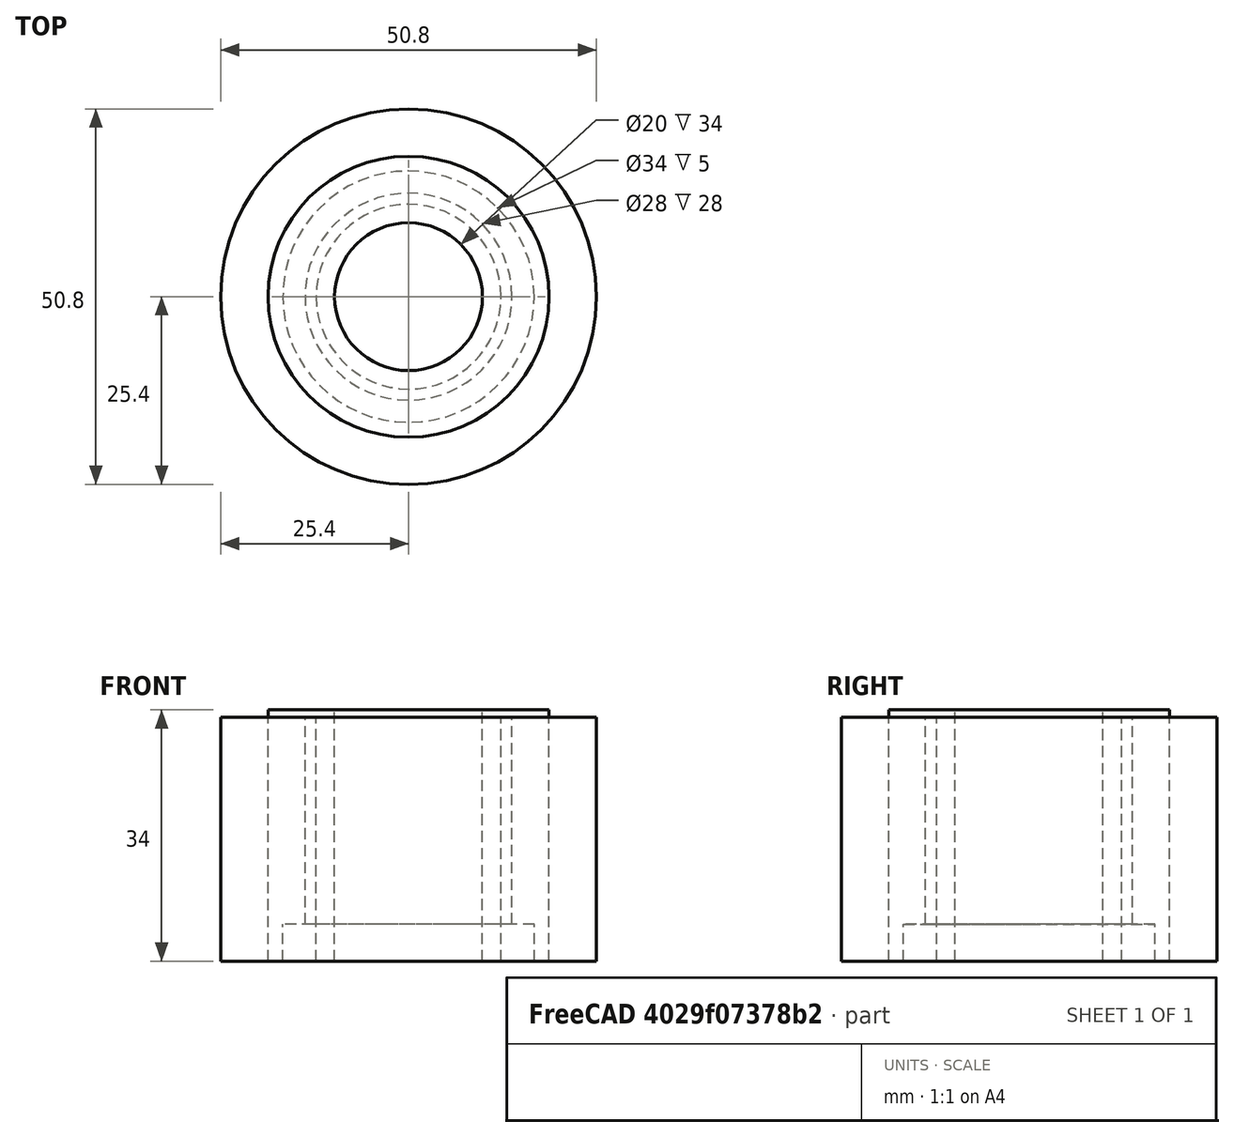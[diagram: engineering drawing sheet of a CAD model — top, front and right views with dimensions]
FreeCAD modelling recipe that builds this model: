
FCSTD DOCUMENT  (FreeCAD 0.17R13509 (Git))
Label: FTInsulator1_larger
License: All rights reserved
LicenseURL: http://en.wikipedia.org/wiki/All_rights_reserved
objects: Part::Cylinder×7, Path::FeaturePython×5, Part::Cut×3, Part::MultiFuse×2, Part::FeaturePython×2, Part::Box×1, App::FeaturePython×1, Path::FeatureCompoundPython×1
note: 18 computed .brp shape members not serialized (recipe doc carries the construction recipe); baked Part::Feature solids carry a one-line shape summary decoded from their .brp

FEATURE [Part::Cylinder] Cylinder084  label="Feedthrough005"
  Angle = 360
  AttacherType = Attacher::AttachEngine3D
  Height = 5
  Placement = pos=(73.66,148,-10) rot=(0,0,1;0rad)
  Radius = 17
  expr: Radius = 17
  expr: Placement.Base.x = 210.81999999999999 / 2 - 31.75
FEATURE [Part::Cylinder] Cylinder088  label="Feedthrough008"
  Angle = 360
  AttacherType = Attacher::AttachEngine3D
  Height = 33
  Placement = pos=(73.66,148,-10) rot=(0,0,1;0rad)
  Radius = 14
  expr: Radius = 28 / 2
  expr: Placement.Base.x = 210.81999999999999 / 2 - 31.75
FEATURE [Part::Cylinder] Cylinder090  label="FTInsInnerHole"
  Angle = 360
  AttacherType = Attacher::AttachEngine3D
  Height = 33
  Placement = pos=(73.66,148,-10) rot=(0,0,1;0rad)
  Radius = 12.5
  expr: Placement.Base.x = 210.81999999999999 / 2 - 31.75
FEATURE [Part::Box] Box016  label="FTInsLug"
  AttacherType = Attacher::AttachEngine3D
  Height = 1
  Length = 1
  Placement = pos=(63,136,-8) rot=(0,0,1;0rad)
  Width = 1
FEATURE [Part::Cylinder] Cylinder093  label="FTInsMount1"
  Angle = 360
  AttacherType = Attacher::AttachEngine3D
  Height = 14
  Placement = pos=(53.66,148,-15) rot=(0,0,1;0rad)
  Radius = 1.5
  expr: Placement.Base.x = 73.659999999999997 - 20
FEATURE [Part::Cylinder] Cylinder094  label="FTInsMount2"
  Angle = 360
  AttacherType = Attacher::AttachEngine3D
  Height = 14
  Placement = pos=(93.66,148,-14) rot=(0,0,1;0rad)
  Radius = 1.5
  expr: Placement.Base.x = 73.659999999999997 + 20
FEATURE [Part::MultiFuse] Fusion038
  Shapes = -> [Cylinder084,Cylinder088,Box016]
FEATURE [Part::MultiFuse] Fusion039
  Shapes = -> [Cylinder094,Cylinder093,Cylinder090]
FEATURE [Part::Cut] Cut010  label="FTInsulator1"
  Base = -> Fusion038
  Placement = pos=(-73.66,-148,-23) rot=(0,0,1;0rad)
  Tool = -> Fusion039
  expr: Placement.Base.z = -33 + 10
FEATURE [App::FeaturePython] SetupSheet  # Path/CAM operation (typed FeaturePython)
  ClearanceHeightExpression = StartDepth+SetupSheet.ClearanceHeightOffset
  ClearanceHeightOffset = 5
  FinalDepthExpression = OpFinalDepth
  HorizRapid = 0
  SafeHeightExpression = StartDepth+SetupSheet.SafeHeightOffset
  SafeHeightOffset = 3
  StartDepthExpression = OpStartDepth
  StepDownExpression = OpToolDiameter
  VertRapid = 0
FEATURE [Part::FeaturePython] Clone  label="Base-FTInsulator1"  # Draft clone (typed FeaturePython)
  AttacherType = Attacher::AttachEngine3D
  Fuse = false
  Objects = -> [Cut010]
  PathResource = Base
  Placement = pos=(-73.66,-148,-23) rot=(0,0,1;0rad)
  Scale = (1,1,1)
FEATURE [Part::FeaturePython] Stock001  # WARN: FeaturePython — macro-defined, semantics opaque (R4)
  Height = 33
  Placement = pos=(0,0,-33) rot=(0,0,1;0rad)
  Radius = 25.4
  StockType = CreateCylinder
FEATURE [Path::FeaturePython] T2__250_End_Mill  label="T2: 250 End Mill"  # Path/CAM operation (typed FeaturePython)
  HorizFeed = 1500
  HorizRapid = 0
  SpindleDir = 0
  SpindleSpeed = 24000
  ToolNumber = 2
  VertFeed = 35
  VertRapid = 0
  expr: HorizRapid = SetupSheet.HorizRapid
  expr: VertRapid = SetupSheet.VertRapid
FEATURE [Path::FeaturePython] Profile_Faces  # Path/CAM operation (typed FeaturePython)
  Active = true
  AreaParams:
    OpenMode = 0
    Angle = 45.0
    MinArcPoints = 4
    Coplanar = 0
    Tolerance = 1e-07
    CleanDistance = 0.0
    PocketExtraOffset = 0.0
    RoundPrecision = 0.0
    AngleShift = 0.0
    SubjectFill = 0
    PocketMode = 0
    Simplify = False
    SectionTolerance = 1e-06
    MaxArcPoints = 100
    Offset = 3.175
    Accuracy = 0.01
    PocketStepover = 0.0
    ClipFill = 0
    ToolRadius = 1.0
    Outline = False
    ClipperScale = 10000000.0
    FromCenter = False
    Explode = False
    EndType = 0
    Shift = 0.0
    ExtraPass = 0
    Project = False
    JoinType = 0
    Thicken = False
    Stepdown = 1.0
    SectionMode = 2
    MiterLimit = 2.0
    Deflection = 0.01
    Reorient = True
    FitArcs = True
    SectionCount = -1
    SectionOffset = 0.0
    Stepover = 0.0
    Unit = 1.0
    Fill = 0
  Base = -> [Clone]
  ClearanceHeight = 5
  Direction = 0
  FinalDepth = -28
  JoinType = 0
  MiterLimit = 0.1
  OffsetExtra = 0
  OpFinalDepth = -28
  OpStartDepth = 0
  OpToolDiameter = 6.35
  PathParams = {'resume_height': 3.0, 'feedrate': 1500.0, 'verbose': True, 'orientation': 1, 'return_end': True, 'preamble': False, 'retraction': 5.0, 'feedrate_v': 35.0}
  SafeHeight = 3
  Side = 0
  StartDepth = 0
  StartPoint = (0,0,0)
  StepDown = 1.5
  ToolController = -> T2__250_End_Mill
  UseComp = true
  UseStartPoint = false
  processCircles = false
  processHoles = false
  processPerimeter = true
  expr: ClearanceHeight = StartDepth + SetupSheet.ClearanceHeightOffset
  expr: SafeHeight = StartDepth + SetupSheet.SafeHeightOffset
  expr: StepDown = 1.5
  expr: FinalDepth = OpFinalDepth
  expr: StartDepth = OpStartDepth
FEATURE [Path::FeaturePython] Profile_Faces001  # Path/CAM operation (typed FeaturePython)
  Active = true
  AreaParams:
    OpenMode = 0
    Angle = 45.0
    MinArcPoints = 4
    Coplanar = 0
    Tolerance = 1e-07
    CleanDistance = 0.0
    PocketExtraOffset = 0.0
    RoundPrecision = 0.0
    AngleShift = 0.0
    SubjectFill = 0
    PocketMode = 0
    Simplify = False
    SectionTolerance = 1e-06
    MaxArcPoints = 100
    Offset = 3.175
    Accuracy = 0.01
    PocketStepover = 0.0
    ClipFill = 0
    ToolRadius = 1.0
    Outline = False
    ClipperScale = 10000000.0
    FromCenter = False
    Explode = False
    EndType = 0
    Shift = 0.0
    ExtraPass = 0
    Project = False
    JoinType = 0
    Thicken = False
    Stepdown = 1.0
    SectionMode = 2
    MiterLimit = 2.0
    Deflection = 0.01
    Reorient = True
    FitArcs = True
    SectionCount = -1
    SectionOffset = 0.0
    Stepover = 0.0
    Unit = 1.0
    Fill = 0
  Base = -> [Clone]
  ClearanceHeight = 5
  Direction = 0
  FinalDepth = -33
  JoinType = 0
  MiterLimit = 0.1
  OffsetExtra = 0
  OpFinalDepth = -33
  OpStartDepth = 0
  OpToolDiameter = 6.35
  PathParams = {'resume_height': 3.0, 'feedrate': 1500.0, 'verbose': True, 'orientation': 1, 'return_end': True, 'preamble': False, 'retraction': 5.0, 'feedrate_v': 35.0}
  SafeHeight = 3
  Side = 0
  StartDepth = 0
  StartPoint = (0,0,0)
  StepDown = 1.5
  ToolController = -> T2__250_End_Mill
  UseComp = true
  UseStartPoint = false
  processCircles = false
  processHoles = false
  processPerimeter = true
  expr: ClearanceHeight = StartDepth + SetupSheet.ClearanceHeightOffset
  expr: SafeHeight = StartDepth + SetupSheet.SafeHeightOffset
  expr: StepDown = 1.5
  expr: FinalDepth = OpFinalDepth
  expr: StartDepth = OpStartDepth
FEATURE [Path::FeaturePython] Pocket_Shape  # Path/CAM operation (typed FeaturePython)
  Active = true
  AreaParams:
    OpenMode = 0
    Angle = 45.0
    MinArcPoints = 4
    Coplanar = 0
    Tolerance = 1e-07
    CleanDistance = 0.0
    PocketExtraOffset = 0.0
    RoundPrecision = 0.0
    AngleShift = 0.0
    SubjectFill = 0
    PocketMode = 3
    Simplify = False
    SectionTolerance = 1e-06
    MaxArcPoints = 100
    Offset = 0.0
    Accuracy = 0.01
    PocketStepover = 3.175
    ClipFill = 0
    ToolRadius = 3.175
    Outline = False
    ClipperScale = 10000000.0
    FromCenter = True
    Explode = False
    EndType = 0
    Shift = 0.0
    ExtraPass = 0
    Project = False
    JoinType = 0
    Thicken = False
    Stepdown = 1.0
    SectionMode = 2
    MiterLimit = 2.0
    Deflection = 0.01
    Reorient = True
    FitArcs = True
    SectionCount = -1
    SectionOffset = 0.0
    Stepover = 0.0
    Unit = 1.0
    Fill = 0
  Base = -> [Clone]
  ClearanceHeight = 5
  CutMode = 0
  ExtraOffset = 0
  FinalDepth = -33
  FinishDepth = 0
  KeepToolDown = false
  MinTravel = false
  OffsetPattern = 2
  OpFinalDepth = -33
  OpStartDepth = 0
  OpToolDiameter = 6.35
  PathParams = {'resume_height': 3.0, 'feedrate': 1500.0, 'verbose': True, 'orientation': 1, 'return_end': True, 'preamble': False, 'retraction': 5.0, 'feedrate_v': 35.0}
  SafeHeight = 3
  StartAt = 0
  StartDepth = 0
  StartPoint = (0,0,0)
  StepDown = 1.5
  StepOver = 50
  ToolController = -> T2__250_End_Mill
  UseStartPoint = false
  ZigZagAngle = 45
  expr: ClearanceHeight = StartDepth + SetupSheet.ClearanceHeightOffset
  expr: SafeHeight = StartDepth + SetupSheet.SafeHeightOffset
  expr: StepDown = 1.5
  expr: FinalDepth = OpFinalDepth
  expr: StartDepth = OpStartDepth
FEATURE [Path::FeatureCompoundPython] Operations  # Path/CAM operation (typed FeaturePython)
  Group = -> [Profile_Faces,Profile_Faces001,Pocket_Shape]
  UsePlacements = false
FEATURE [Path::FeaturePython] Job  # Path/CAM operation (typed FeaturePython)
  Base = -> Clone
  GeometryTolerance = 0.01
  Operations = -> Operations
  PostProcessor = 5
  PostProcessorOutputFile = <userpath>/Documents/CNC/chamber_plate/fts/ftinsulator1_new_250_roughing.ngc
  SetupSheet = -> SetupSheet
  Stock = -> Stock001
  ToolController = -> [T2__250_End_Mill]
FEATURE [Part::Cylinder] Cylinder
  Angle = 360
  AttacherType = Attacher::AttachEngine3D
  Height = 34
  Placement = pos=(0,0,-33) rot=(0,0,1;0rad)
  Radius = 19
FEATURE [Part::Cut] Cut
  Base = -> Cylinder
  Tool = -> Cut010
FEATURE [Part::Cylinder] Cylinder095  label="Cylinder001"
  Angle = 360
  AttacherType = Attacher::AttachEngine3D
  Height = 34
  Placement = pos=(0,0,-33) rot=(0,0,1;0rad)
  Radius = 10
FEATURE [Part::Cut] Cut011
  Base = -> Cut
  Tool = -> Cylinder095
